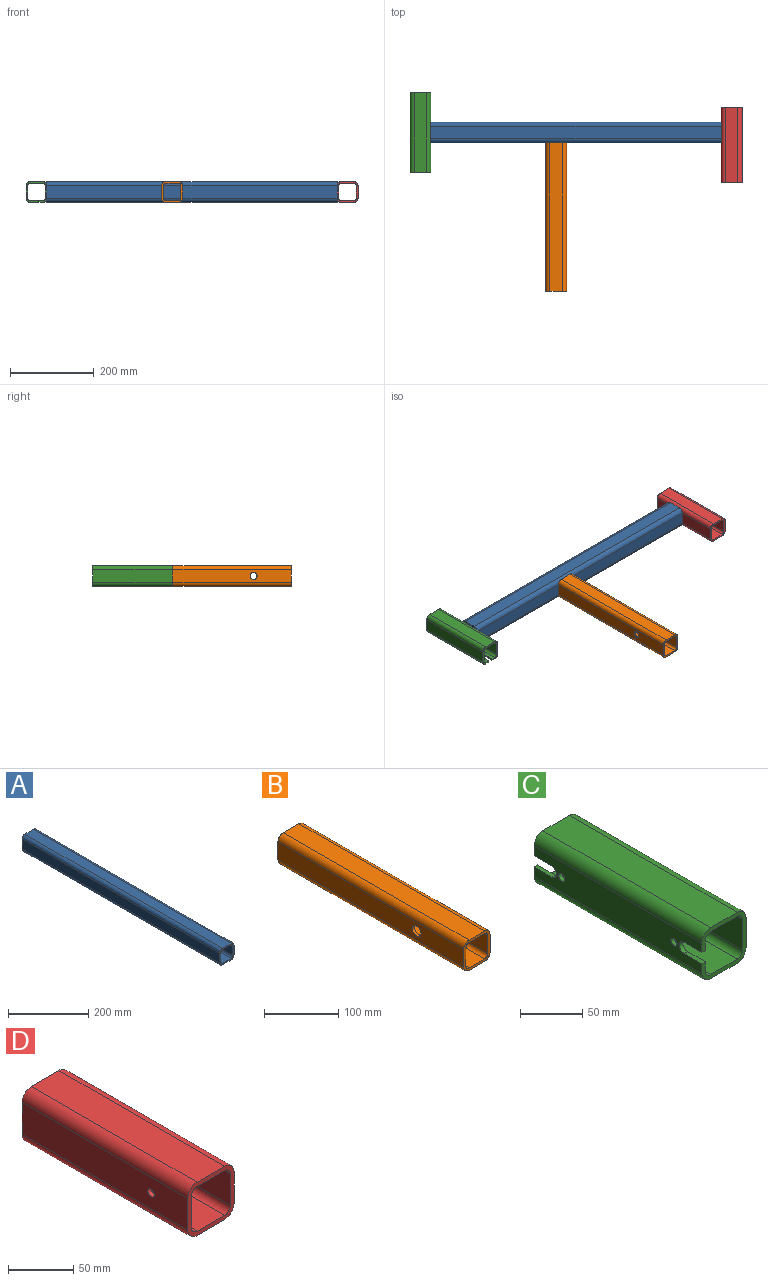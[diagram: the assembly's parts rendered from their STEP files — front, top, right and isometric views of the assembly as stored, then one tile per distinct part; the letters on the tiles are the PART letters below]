
ASSEMBLY  parts=4 mates=3
PART A: 18 faces, bbox 50x695x50 mm
  f0: plane 695x30mm, normal (1,0,0), area 20850mm2, adj f4,f5,f6,f9
  f1: plane 695x30mm, normal (0,0,1), area 20850mm2, adj f4,f5,f6,f7
  f2: plane 695x30mm, normal (-1,0,0), area 20850mm2, adj f4,f5,f7,f8
  f3: plane 695x30mm, normal (0,0,-1), area 20850mm2, adj f4,f5,f8,f9
  f4: plane 50x50mm, normal (0,-1,0), area 681.1mm2, adj f0,f1,f2,f3,f6,f7,f8,f9
  f5: plane 50x50mm, normal (0,1,0), area 681.1mm2, adj f0,f1,f2,f3,f6,f7,f8,f9
  f6: cylinder r=10mm len=695mm, axis (0,-1,0), area 10917mm2, adj f0,f1,f4,f5
  f7: cylinder r=10mm len=695mm, axis (0,1,0), area 10917mm2, adj f1,f2,f4,f5
  f8: cylinder r=10mm len=695mm, axis (0,-1,0), area 10917mm2, adj f2,f3,f4,f5
  f9: cylinder r=10mm len=695mm, axis (0,1,0), area 10917mm2, adj f0,f3,f4,f5
  f10: plane 695x30mm, normal (-1,0,0), area 20850mm2, adj f4,f5,f11,f17
  f11: cylinder r=6mm len=695mm, axis (0,-1,0), area 6550.2mm2, adj f4,f5,f10,f12
  f12: plane 695x30mm, normal (0,0,-1), area 20850mm2, adj f4,f5,f11,f13
  f13: cylinder r=6mm len=695mm, axis (0,-1,0), area 6550.2mm2, adj f4,f5,f12,f14
  f14: plane 695x30mm, normal (1,0,0), area 20850mm2, adj f4,f5,f13,f15
  f15: cylinder r=6mm len=695mm, axis (0,-1,0), area 6550.2mm2, adj f4,f5,f14,f16
  f16: plane 695x30mm, normal (0,0,1), area 20850mm2, adj f4,f5,f15,f17
  f17: cylinder r=6mm len=695mm, axis (0,-1,0), area 6550.2mm2, adj f4,f5,f10,f16
PART B: 20 faces, bbox 50x355x50 mm
  f0: plane 355x30mm, normal (1,0,0), area 10436.2mm2, adj f4,f5,f6,f9,f19
  f1: plane 355x30mm, normal (0,0,1), area 10650mm2, adj f4,f5,f6,f7
  f2: plane 355x30mm, normal (-1,0,0), area 10436.2mm2, adj f4,f5,f7,f8,f18
  f3: plane 355x30mm, normal (0,0,-1), area 10650mm2, adj f4,f5,f8,f9
  f4: plane 50x50mm, normal (0,-1,0), area 681.1mm2, adj f0,f1,f2,f3,f6,f7,f8,f9
  f5: plane 50x50mm, normal (0,1,0), area 681.1mm2, adj f0,f1,f2,f3,f6,f7,f8,f9
  f6: cylinder r=10mm len=355mm, axis (0,-1,0), area 5576.3mm2, adj f0,f1,f4,f5
  f7: cylinder r=10mm len=355mm, axis (0,1,0), area 5576.3mm2, adj f1,f2,f4,f5
  f8: cylinder r=10mm len=355mm, axis (0,-1,0), area 5576.3mm2, adj f2,f3,f4,f5
  f9: cylinder r=10mm len=355mm, axis (0,1,0), area 5576.3mm2, adj f0,f3,f4,f5
  f10: plane 355x30mm, normal (-1,0,0), area 10436.2mm2, adj f4,f5,f11,f17,f19
  f11: cylinder r=6mm len=355mm, axis (0,-1,0), area 3345.8mm2, adj f4,f5,f10,f12
  f12: plane 355x30mm, normal (0,0,-1), area 10650mm2, adj f4,f5,f11,f13
  f13: cylinder r=6mm len=355mm, axis (0,-1,0), area 3345.8mm2, adj f4,f5,f12,f14
  f14: plane 355x30mm, normal (1,0,0), area 10436.2mm2, adj f4,f5,f13,f15,f18
  f15: cylinder r=6mm len=355mm, axis (0,-1,0), area 3345.8mm2, adj f4,f5,f14,f16
  f16: plane 355x30mm, normal (0,0,1), area 10650mm2, adj f4,f5,f15,f17
  f17: cylinder r=6mm len=355mm, axis (0,-1,0), area 3345.8mm2, adj f4,f5,f10,f16
  f18: cylinder r=8.25mm len=16.5mm, axis (-1,0,0), area 207.3mm2, adj f2,f14
  f19: cylinder r=8.25mm len=16.5mm, axis (-1,0,0), area 207.3mm2, adj f0,f10
PART C: 26 faces, bbox 50x190x50 mm
  f0: plane 190x30mm, normal (-1,0,0), area 5088mm2, adj f2,f6,f7,f10,f18,f19,f20,f21
  f1: plane 190x30mm, normal (1,0,0), area 5088mm2, adj f2,f6,f11,f17,f18,f19,f20,f21
  f2: plane 50x50mm, normal (0,1,0), area 637.1mm2, adj f0,f1,f3,f4,f5,f7,f8,f9
  f3: plane 190x30mm, normal (0,0,-1), area 5700mm2, adj f2,f6,f7,f8
  f4: plane 190x30mm, normal (1,0,0), area 5700mm2, adj f2,f6,f8,f9
  f5: plane 190x30mm, normal (0,0,1), area 5700mm2, adj f2,f6,f9,f10
  f6: plane 50x50mm, normal (0,-1,0), area 637.1mm2, adj f0,f1,f3,f4,f5,f7,f8,f9
  f7: cylinder r=10mm len=190mm, axis (0,-1,0), area 2984.5mm2, adj f0,f2,f3,f6
  f8: cylinder r=10mm len=190mm, axis (0,-1,0), area 2984.5mm2, adj f2,f3,f4,f6
  f9: cylinder r=10mm len=190mm, axis (0,1,0), area 2984.5mm2, adj f2,f4,f5,f6
  f10: cylinder r=10mm len=190mm, axis (0,1,0), area 2984.5mm2, adj f0,f2,f5,f6
  f11: cylinder r=6mm len=190mm, axis (0,-1,0), area 1790.7mm2, adj f1,f2,f6,f12
  f12: plane 190x30mm, normal (0,0,1), area 5700mm2, adj f2,f6,f11,f13
  f13: cylinder r=6mm len=190mm, axis (0,-1,0), area 1790.7mm2, adj f2,f6,f12,f14
  f14: plane 190x30mm, normal (-1,0,0), area 5700mm2, adj f2,f6,f13,f15
  f15: cylinder r=6mm len=190mm, axis (0,-1,0), area 1790.7mm2, adj f2,f6,f14,f16
  f16: plane 190x30mm, normal (0,0,-1), area 5700mm2, adj f2,f6,f15,f17
  f17: cylinder r=6mm len=190mm, axis (0,-1,0), area 1790.7mm2, adj f1,f2,f6,f16
  f18: plane 20x4mm, normal (0,0,1), area 80mm2, adj f0,f1,f2,f19
  f19: cylinder r=5.5mm len=11mm, axis (-1,0,0), area 69.1mm2, adj f0,f1,f18,f20
  f20: plane 20x4mm, normal (0,0,-1), area 80mm2, adj f0,f1,f2,f19
  f21: cylinder r=3.5mm len=7mm, axis (-1,0,0), area 88mm2, adj f0,f1
  f22: plane 20x4mm, normal (0,0,-1), area 80mm2, adj f0,f1,f6,f23
  f23: cylinder r=5.5mm len=11mm, axis (-1,0,0), area 69.1mm2, adj f0,f1,f22,f24
  f24: plane 20x4mm, normal (0,0,1), area 80mm2, adj f0,f1,f6,f23
  f25: cylinder r=3.5mm len=7mm, axis (-1,0,0), area 88mm2, adj f0,f1
PART D: 19 faces, bbox 50x180x50 mm
  f0: plane 180x30mm, normal (-1,0,0), area 5361.5mm2, adj f4,f5,f6,f9,f18
  f1: plane 180x30mm, normal (0,0,-1), area 5400mm2, adj f4,f5,f6,f7
  f2: plane 180x30mm, normal (1,0,0), area 5400mm2, adj f4,f5,f7,f8
  f3: plane 180x30mm, normal (0,0,1), area 5400mm2, adj f4,f5,f8,f9
  f4: plane 50x50mm, normal (0,-1,0), area 681.1mm2, adj f0,f1,f2,f3,f6,f7,f8,f9
  f5: plane 50x50mm, normal (0,1,0), area 681.1mm2, adj f0,f1,f2,f3,f6,f7,f8,f9
  f6: cylinder r=10mm len=180mm, axis (0,-1,0), area 2827.4mm2, adj f0,f1,f4,f5
  f7: cylinder r=10mm len=180mm, axis (0,-1,0), area 2827.4mm2, adj f1,f2,f4,f5
  f8: cylinder r=10mm len=180mm, axis (0,1,0), area 2827.4mm2, adj f2,f3,f4,f5
  f9: cylinder r=10mm len=180mm, axis (0,1,0), area 2827.4mm2, adj f0,f3,f4,f5
  f10: plane 180x30mm, normal (1,0,0), area 5361.5mm2, adj f4,f5,f11,f17,f18
  f11: cylinder r=6mm len=180mm, axis (0,-1,0), area 1696.5mm2, adj f4,f5,f10,f12
  f12: plane 180x30mm, normal (0,0,1), area 5400mm2, adj f4,f5,f11,f13
  f13: cylinder r=6mm len=180mm, axis (0,-1,0), area 1696.5mm2, adj f4,f5,f12,f14
  f14: plane 180x30mm, normal (-1,0,0), area 5400mm2, adj f4,f5,f13,f15
  f15: cylinder r=6mm len=180mm, axis (0,-1,0), area 1696.5mm2, adj f4,f5,f14,f16
  f16: plane 180x30mm, normal (0,0,-1), area 5400mm2, adj f4,f5,f15,f17
  f17: cylinder r=6mm len=180mm, axis (0,-1,0), area 1696.5mm2, adj f4,f5,f10,f16
  f18: cylinder r=3.5mm len=7mm, axis (-1,0,0), area 88mm2, adj f0,f10
PLACE A rot(axis=(0.71,0.71,0),180deg) t=(47.5,25,0)mm
PLACE B at identity fixed
PLACE C rot(axis=(0.71,0,0.71),180deg) t=(-350,25,-25)mm
PLACE D rot(axis=(0,-1,0),90deg) t=(445,85,-25)mm
MATE fastened A.f4 <-> C.f5  axis (-1,0,0) through (-300,25,0)mm
MATE fastened D.f3 <-> A.f5  axis (-1,0,0) through (395,-5,0)mm
MATE fastened B.f5 <-> A.f2  axis (0,1,0) through (0,0,0)mm
